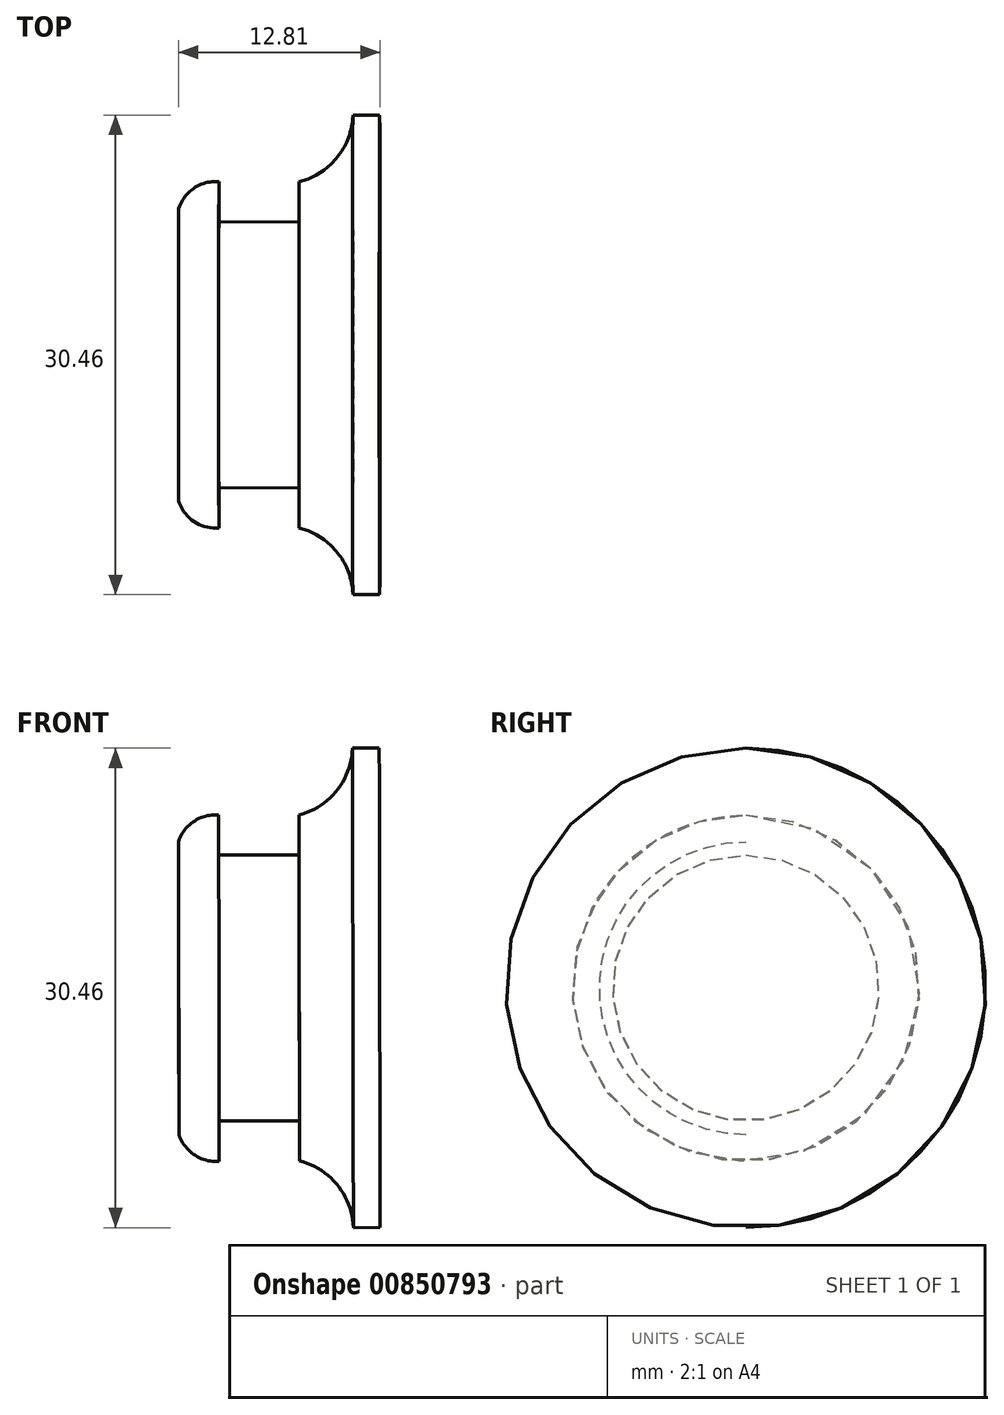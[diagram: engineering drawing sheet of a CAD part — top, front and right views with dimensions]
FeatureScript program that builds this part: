
annotation { "Feature Type Name" : "Feature", "Feature Type Description" : "" }
export const myFeature = defineFeature(function(context is Context, id is Id, definition is map)
    precondition{}
    {
        {
            var Q0;
            Q0=qCreatedBy(makeId("Front.planeOp"),FACE);
            var sketch = newSketch(context, id + "F0", { "sketchPlane" : qUnion([Q0])});
            skLineSegment(sketch, "E0", {"start": v(0, 0) * mm, "end": v(0, 9) * mm});
            skLineSegment(sketch, "E1", {"start": v(0, 9) * mm, "end": v(-1, 9) * mm});
            skLineSegment(sketch, "E2", {"start": v(-3, 6.5) * mm, "end": v(-3, 5) * mm});
            skLineSegment(sketch, "E3", {"start": v(-3, 5) * mm, "end": v(-6, 5) * mm});
            skLineSegment(sketch, "E4", {"start": v(-6, 5) * mm, "end": v(-6, 6.5) * mm});
            skPoint(sketch, "E5", {"position": v(-1, 7.75) * mm});
            skPoint(sketch, "E6", {"position": v(-2, 6.5) * mm});
            skPoint(sketch, "E7", {"position": v(-6.75, 6.5) * mm});
            skLineSegment(sketch, "E8", {"start": v(-7.5, 5.5) * mm, "end": v(-7.5, 0) * mm});
            skLineSegment(sketch, "E9", {"start": v(-7.5, 0) * mm, "end": v(0, 0) * mm});
            skPoint(sketch, "E10.trimOffspring.end.orphan", {"position": v(-7.5, 6.5) * mm});
            skPoint(sketch, "E11.orphan", {"position": v(-1, 6.5) * mm});
            skLineSegment(sketch, "E12", {"start": v(-22.96, 0) * mm, "end": v(0.04, 0.04) * mm});
            skArc(sketch, "E13", {"start": v(-7.39, 0) * mm, "mid": v(-7.39, 0.01) * mm, "end": v(-7.39, 0.03) * mm});
            skPoint(sketch, "E13.third.point", {"position": v(-11.01, 6.6) * mm});
            skLineSegment(sketch, "E14", {"start": v(-22.96, 0) * mm, "end": v(-15.36, 0.01) * mm});
            skLineSegment(sketch, "E15", {"start": v(-16.46, 7.53) * mm, "end": v(-16.46, 6.53) * mm});
            skArc(sketch, "E16", {"start": v(-11.86, 3.43) * mm, "mid": v(-13.58, 5.85) * mm, "end": v(-16.46, 6.53) * mm});
            skPoint(sketch, "E16.third.point", {"position": v(-15.11, -1.74) * mm});
            skArc(sketch, "E17.trimOffspring", {"start": v(-16.46, 7.53) * mm, "mid": v(-21.12, 4.98) * mm, "end": v(-22.96, 0) * mm});
            skArc(sketch, "E18", {"start": v(-6, 6.5) * mm, "mid": v(-6.93, 6.26) * mm, "end": v(-7.5, 5.5) * mm});
            skArc(sketch, "E19", {"start": v(-11.86, 3.43) * mm, "mid": v(-9.37, 3.81) * mm, "end": v(-7.5, 5.5) * mm});
            skArc(sketch, "E20", {"start": v(-3, 6.5) * mm, "mid": v(-1.58, 7.42) * mm, "end": v(-1, 9) * mm});
            skSolve(sketch);
        }
        {
            var Q0;
            {var subQ9=sQuery(id+"F0.wireOp",EDGE,"E1");Q0=makeQuery(id+"F0.imprint","IMPRINT",FACE,{"disambiguationData":[TD([[makeQuery(id+"F0.imprint","IMPRINT",EDGE,{"derivedFrom":subQ9}),1.0]])]});}
            var Q1;
            {var subQ0=sQuery(id+"F0.wireOp",EDGE,"E14");Q1=makeQuery(id+"F0.imprint","IMPRINT",FACE,{"disambiguationData":[TD([[makeQuery(id+"F0.imprint","IMPRINT",EDGE,{"derivedFrom":subQ0}),1.0]])]});}
            var Q2;
            {var subQ0=sQuery(id+"F0.wireOp",EDGE,"E19");var subQ1=sQuery(id+"F0.wireOp",EDGE,"b3faeed5-2eac-4132-92e8-650fd7fe0288");var subQ2=makeQuery(id+"F0.imprint","INTERSECT",VERTEX,{"disambiguationData":[OD(0.0)],"derivedFrom":[subQ1,subQ0]});Q2=makeQuery(id+"F0.imprint","IMPRINT",FACE,{"disambiguationData":[TD([[makeQuery(id+"F0.imprint","IMPRINT",EDGE,{"disambiguationData":[TD([[subQ2,-1.0]])],"derivedFrom":subQ1}),-1.0]])]});}
            var Q3;
            Q3=sQuery(id+"F0.wireOp",EDGE,"E12");
            revolve(context, id + "F1", {"entities" : qUnion([Q0, Q1, Q2]), "axis" : qUnion([Q3]), "revolveType" : RevolveType.FULL});
        }
        {
            var Q0;
            Q0=makeQuery(id+"F1.opRevolve","SWEPT_BODY",BODY,{"disambiguationData":[OSD([sQuery(id+"F0.wireOp",EDGE,"E0"),sQuery(id+"F0.wireOp",EDGE,"E1"),sQuery(id+"F0.wireOp",EDGE,"E2"),sQuery(id+"F0.wireOp",EDGE,"E3"),sQuery(id+"F0.wireOp",EDGE,"E4"),sQuery(id+"F0.wireOp",EDGE,"c7e0a1e9-a911-4932-8d18-88bd7e0dbcae"),sQuery(id+"F0.wireOp",EDGE,"fead766b-27d7-461d-9200-e427df9684da"),sQuery(id+"F0.wireOp",EDGE,"E12"),sQuery(id+"F0.wireOp",EDGE,"b3faeed5-2eac-4132-92e8-650fd7fe0288"),sQuery(id+"F0.wireOp",EDGE,"E14"),sQuery(id+"F0.wireOp",EDGE,"E15"),sQuery(id+"F0.wireOp",EDGE,"E16"),sQuery(id+"F0.wireOp",EDGE,"E17.trimOffspring")])]});
            var Q1;
            Q1=qCreatedBy(makeId("Origin.pointOp"),VERTEX);
            transform(context, id + "F2", {"entities" : qUnion([Q0]), "transformType" : TransformType.SCALE_UNIFORMLY, "scale" : 1.7, "scalePoint" : qUnion([Q1]), "makeCopy" : true});
        }
        {
            var Q0;
            Q0=makeQuery(id+"F1.opRevolve","SWEPT_BODY",BODY,{"disambiguationData":[OSD([sQuery(id+"F0.wireOp",EDGE,"E0"),sQuery(id+"F0.wireOp",EDGE,"E1"),sQuery(id+"F0.wireOp",EDGE,"E2"),sQuery(id+"F0.wireOp",EDGE,"E3"),sQuery(id+"F0.wireOp",EDGE,"E4"),sQuery(id+"F0.wireOp",EDGE,"c7e0a1e9-a911-4932-8d18-88bd7e0dbcae"),sQuery(id+"F0.wireOp",EDGE,"fead766b-27d7-461d-9200-e427df9684da"),sQuery(id+"F0.wireOp",EDGE,"E12"),sQuery(id+"F0.wireOp",EDGE,"b3faeed5-2eac-4132-92e8-650fd7fe0288"),sQuery(id+"F0.wireOp",EDGE,"E14"),sQuery(id+"F0.wireOp",EDGE,"E15"),sQuery(id+"F0.wireOp",EDGE,"E16"),sQuery(id+"F0.wireOp",EDGE,"E17.trimOffspring")])]});
            deleteBodies(context, id + "F3", {"entities" : qUnion([Q0])});
        }
    });
